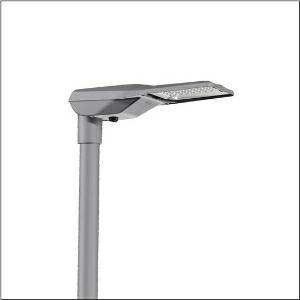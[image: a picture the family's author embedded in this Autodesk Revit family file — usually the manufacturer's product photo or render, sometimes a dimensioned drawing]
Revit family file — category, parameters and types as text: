
# Revit family: streetlight_sl_21_mini___st1_0a_5xe2d33r08jb_72c4
name_source: partatom
category: Lighting Fixtures
units: mm (PartAtom-declared; Revit-internal decimal feet)

## family parameters
Cut with Voids When Loaded = No
Host = Face
Light Source = No
Part Type = Normal
Room Calculation Point = No
Round Connector Dimension = Use Diameter
Shared = No

## types (1)
- --- (1 x LED, 12830 lm, 87.3 W, 3000K)
    Apparent Load = 87 VA
    CIE Flux Codes = 40 73 97 100 100
    Color Rendering = 70
    Color Temperature = 3000K
    Default Elevation = 1800 mm
    Description = Streetlight SL 21 mini, mast luminaire, primary light control with lens, of PMMA, primary optical cover: cover, of toughened safety glass, transparent, light distribution: ST1.0a, light emission: direct distribution, primary light characteristic: asymmetric, installation type: side-entry, post-top, LED, High Power LED, rated luminous flux: 12.830lm, luminous efficacy: 147lm/W, light colour: 730, colour temperature: 3000K, control gear: ECG Smart Interface, control: flexible luminous flux parameterisation, time-dependent luminous flux control, constant luminous flux control, overheat protection, mains connection: 220..240V, AC, 50/60Hz, start of lifetime: 87W, end of lifetime: 90W, reduction: 40W, luminaire housing, of diecast aluminium, powder-coated, Siteco® metallic grey (DB 702S), corrosivity category C5 according to DIN EN ISO 12944, length: 628mm, width: 235mm, height: 110mm, spigot size: 60/76mm (post-top) and 42/60/76mm (side-entry), mast flange for spigot size: 42mm: 5XC10008XM4, 60mm: 5XC10008XM2, 76/60mm: 5XC10108XM1, protection rating (complete): IP66, insulation class (complete): insulation class II (safety insulation), certification: CE, ENEC, VDE, impact resistance: IK09, permissible operating ambient temperature for outdoor applications: -40..+50°C, standard-compliant lighting for roads and squares, packaging unit: 1 piece

Light Distribution: ST1.0a
    Height = 110 mm
    Lamp = 1 x LED
    Lamp Light Flux = 12830 lm
    Lamp Power = 87.3 W
    Lamp count = 1
    Length = 625 mm
    Luminous efficacy = 147 lm/W
    Manufacturer = Siteco
    ModVariant = No
    Model = 5XE2D33R08JB
    Number of Poles = 1
    OnlyDefault = Yes
    Power Factor = 1
    Product Name = Streetlight SL 21 mini | ST1.0a
    Product group = mast luminaire | pylon top
    ProductGroupID = 6100
    Protection Class = Protection class II
    Protection Degree = IP 66
    RLX_Detail_Level = 1
    RlxData = <blob elided: 92241 chars, md5=23bb52a2>
    Socket = socket
    Standby Power = 0 W
    System Light Flux = 12830 lm
    System Power = 87 W
    Type Comments = factory setting: luminous flux: 100 % | dim-lin: 254 | 915 mA
    Type Image = l_1003516.jpg
    URL = http://relux.com
    VarID = @adj_083137
    Voltage = 0 V
    Weight = 0.00 kg
    Width = 234 mm

## geometry (parser evidence)
native form markers: Blend x4, Sweep x10
no freeform markers — native parametric forms only
